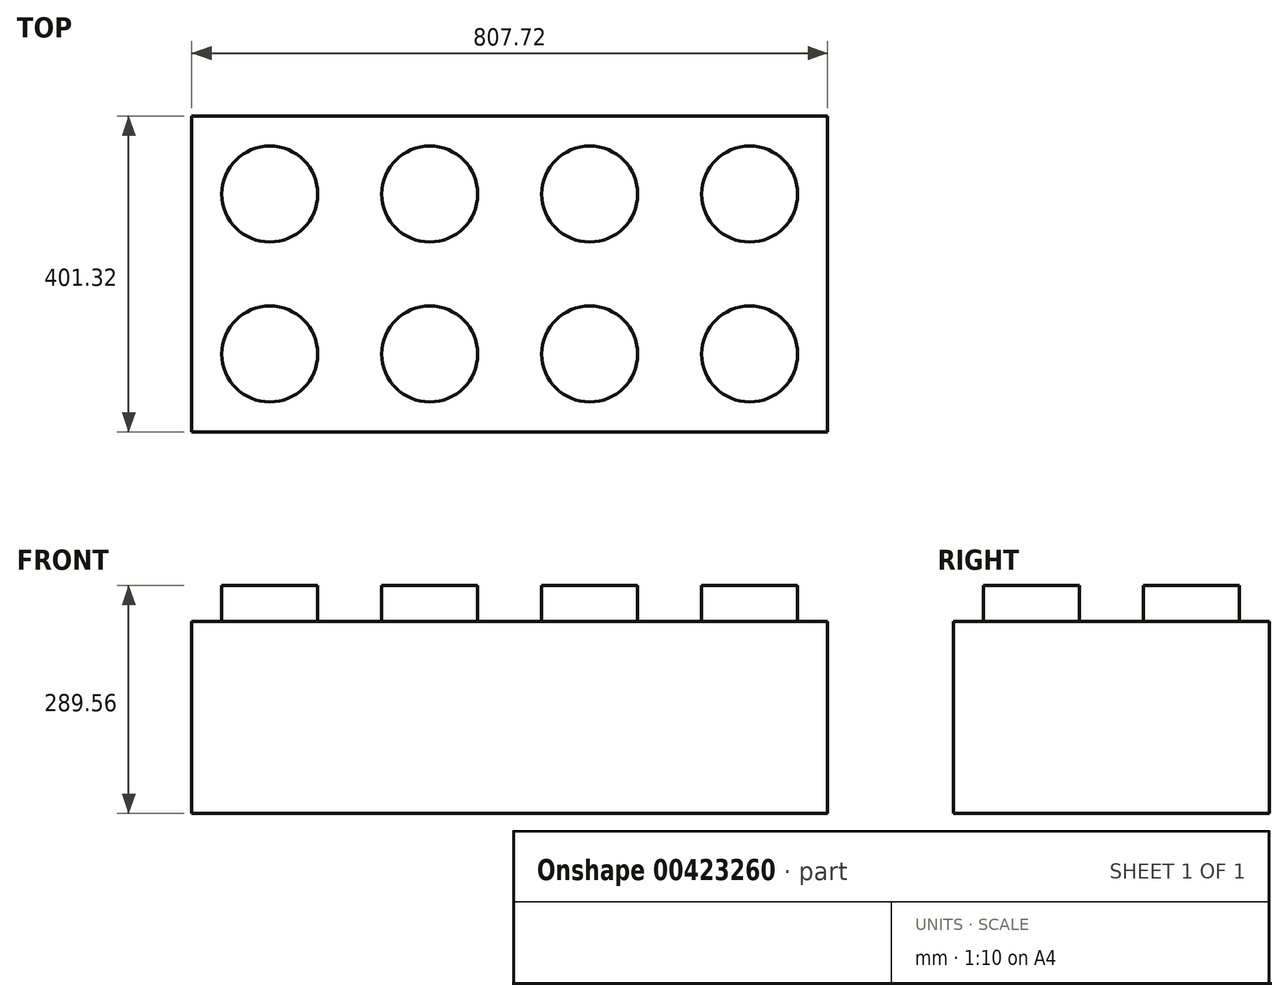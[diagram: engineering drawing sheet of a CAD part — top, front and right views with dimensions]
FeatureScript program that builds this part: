
annotation { "Feature Type Name" : "Feature", "Feature Type Description" : "" }
export const myFeature = defineFeature(function(context is Context, id is Id, definition is map)
    precondition{}
    {
        {
            var Q0;
            Q0=qCreatedBy(makeId("Top.planeOp"),FACE);
            var sketch = newSketch(context, id + "F0", { "sketchPlane" : qUnion([Q0])});
            skLineSegment(sketch, "E0.bottom", {"start": v(-40.29, 348.02) * mm, "end": v(767.43, 348.02) * mm});
            skLineSegment(sketch, "E0.top", {"start": v(-40.29, -53.3) * mm, "end": v(767.43, -53.3) * mm});
            skLineSegment(sketch, "E0.left", {"start": v(-40.29, 348.02) * mm, "end": v(-40.29, -53.3) * mm});
            skLineSegment(sketch, "E0.right", {"start": v(767.43, 348.02) * mm, "end": v(767.43, -53.3) * mm});
            skSolve(sketch);
        }
        {
            var Q0;
            Q0=makeQuery(id+"F0.imprint","IMPRINT",FACE,{"disambiguationData":[TD([[makeQuery(id+"F0.imprint","IMPRINT",EDGE,{"derivedFrom":sQuery(id+"F0.wireOp",EDGE,"E0.bottom")}),-1.0]])]});
            extrude(context, id + "F1", {"entities" : qUnion([Q0]), "depth" : 243.84 * mm});
        }
        {
            var Q0;
            Q0=makeQuery(id+"F1.opExtrude","CAP_FACE",FACE,{"disambiguationData":[OSD([sQuery(id+"F0.wireOp",EDGE,"E0.bottom"),sQuery(id+"F0.wireOp",EDGE,"E0.top"),sQuery(id+"F0.wireOp",EDGE,"E0.left"),sQuery(id+"F0.wireOp",EDGE,"E0.right")])],"isStart":false});
            var sketch = newSketch(context, id + "F2", { "sketchPlane" : qUnion([Q0])});
            skCircle(sketch, "E1", {"center": v(58.77, 45.76) * mm, "radius": 60.96 * mm});
            skCircle(sketch, "E2.0.1.0", {"center": v(58.77, 248.96) * mm, "radius": 60.96 * mm});
            skCircle(sketch, "E2.1.0.0", {"center": v(261.97, 45.76) * mm, "radius": 60.96 * mm});
            skCircle(sketch, "E2.1.1.0", {"center": v(261.97, 248.96) * mm, "radius": 60.96 * mm});
            skCircle(sketch, "E2.2.0.0", {"center": v(465.17, 45.76) * mm, "radius": 60.96 * mm});
            skCircle(sketch, "E2.2.1.0", {"center": v(465.17, 248.96) * mm, "radius": 60.96 * mm});
            skLineSegment(sketch, "E2.direction1", {"start": v(58.77, 45.76) * mm, "end": v(261.97, 45.76) * mm, "construction": true});
            skLineSegment(sketch, "E2.direction2", {"start": v(58.77, 45.76) * mm, "end": v(58.77, 248.96) * mm, "construction": true});
            skCircle(sketch, "E3.0.3.0", {"center": v(668.37, 45.76) * mm, "radius": 60.96 * mm});
            skCircle(sketch, "E3.0.3.1", {"center": v(668.37, 248.96) * mm, "radius": 60.96 * mm});
            skSolve(sketch);
        }
        {
            var Q0;
            Q0 = qSketchRegion(id + "F2", true);
            extrude(context, id + "F3", {"entities" : qUnion([Q0]), "operationType" : NewBodyOperationType.ADD, "depth" : 45.72 * mm});
        }
    });
